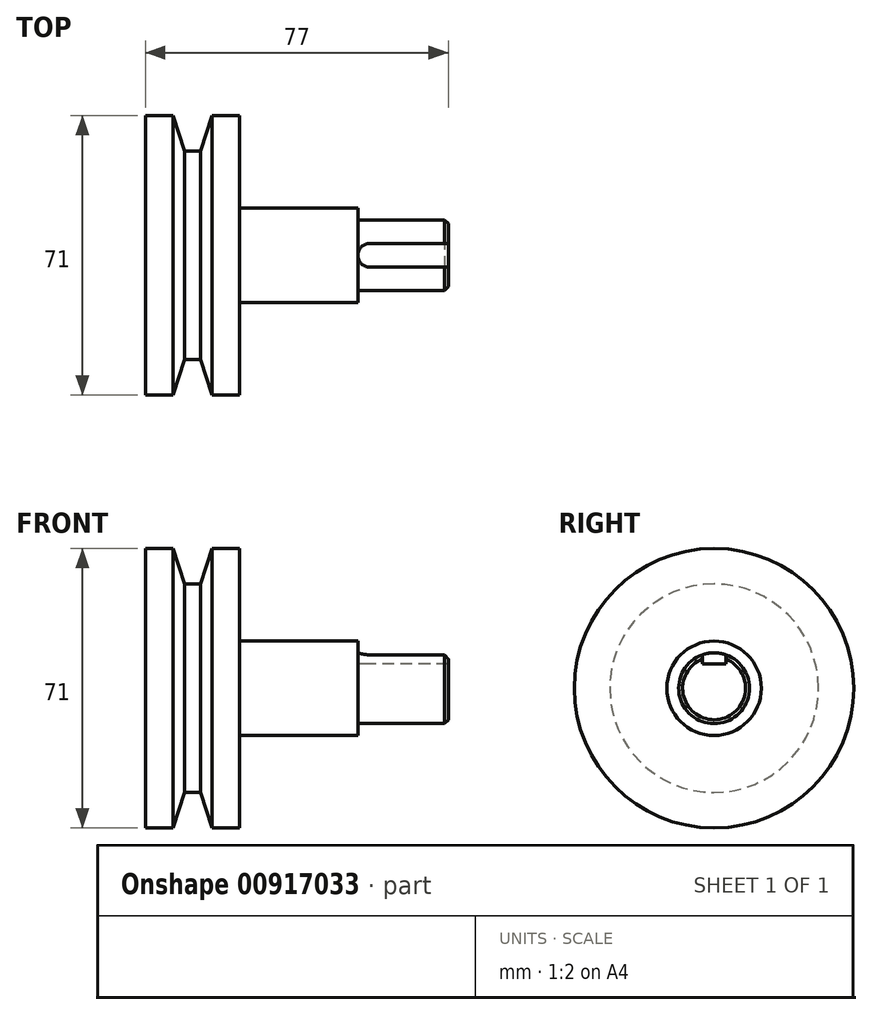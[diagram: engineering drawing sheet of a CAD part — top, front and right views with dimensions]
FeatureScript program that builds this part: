
annotation { "Feature Type Name" : "Feature", "Feature Type Description" : "" }
export const myFeature = defineFeature(function(context is Context, id is Id, definition is map)
    precondition{}
    {
        {
            var Q0;
            Q0=qCreatedBy(makeId("Front.planeOp"),FACE);
            var sketch = newSketch(context, id + "F0", { "sketchPlane" : qUnion([Q0])});
            skLineSegment(sketch, "E0", {"start": v(0, 0) * mm, "end": v(77, 0) * mm});
            skLineSegment(sketch, "E1", {"start": v(77, 0) * mm, "end": v(77, 9) * mm});
            skLineSegment(sketch, "E2", {"start": v(77, 9) * mm, "end": v(54, 9) * mm});
            skLineSegment(sketch, "E3", {"start": v(54, 9) * mm, "end": v(54, 12) * mm});
            skLineSegment(sketch, "E4", {"start": v(54, 12) * mm, "end": v(24, 12) * mm});
            skLineSegment(sketch, "E5", {"start": v(24, 12) * mm, "end": v(24, 35.5) * mm});
            skLineSegment(sketch, "E6", {"start": v(24, 35.5) * mm, "end": v(16.92, 35.5) * mm});
            skLineSegment(sketch, "E7", {"start": v(16.92, 35.5) * mm, "end": v(14, 26.5) * mm});
            skLineSegment(sketch, "E8", {"start": v(14, 26.5) * mm, "end": v(10, 26.5) * mm});
            skLineSegment(sketch, "E9", {"start": v(10, 26.5) * mm, "end": v(7.08, 35.5) * mm});
            skLineSegment(sketch, "E10", {"start": v(7.08, 35.5) * mm, "end": v(0, 35.5) * mm});
            skLineSegment(sketch, "E11", {"start": v(0, 35.5) * mm, "end": v(0, 0) * mm});
            skSolve(sketch);
        }
        {
            var Q0;
            Q0=makeQuery(id+"F0.imprint","IMPRINT",FACE,{"disambiguationData":[TD([[makeQuery(id+"F0.imprint","IMPRINT",EDGE,{"derivedFrom":sQuery(id+"F0.wireOp",EDGE,"E0")}),1.0]])]});
            var Q1;
            Q1=sQuery(id+"F0.wireOp",EDGE,"E0");
            revolve(context, id + "F1", {"surfaceOperationType" : NewSurfaceOperationType.NEW, "entities" : qUnion([Q0]), "axis" : qUnion([Q1]), "revolveType" : RevolveType.FULL});
        }
        {
            var Q0;
            Q0=qCreatedBy(makeId("Top.planeOp"),FACE);
            cPlane(context, id + "F2", {"entities" : qUnion([Q0]), "cplaneType" : CPlaneType.OFFSET, "offset" : 9 * mm, "width" : 150 * mm, "height" : 150 * mm});
        }
        {
            var Q0;
            Q0=qCreatedBy(id+"F2.planeOp",FACE);
            var sketch = newSketch(context, id + "F3", { "sketchPlane" : qUnion([Q0])});
            skLineSegment(sketch, "E12", {"start": v(77, -3) * mm, "end": v(77, 3) * mm});
            skLineSegment(sketch, "E13", {"start": v(77, 3) * mm, "end": v(57, 3) * mm});
            skLineSegment(sketch, "E14", {"start": v(77, -3) * mm, "end": v(57, -3) * mm});
            skArc(sketch, "E15", {"start": v(57, 3) * mm, "mid": v(54, 0) * mm, "end": v(57, -3) * mm});
            skSolve(sketch);
        }
        {
            var Q0;
            Q0=makeQuery(id+"F3.imprint","IMPRINT",FACE,{"disambiguationData":[TD([[makeQuery(id+"F3.imprint","IMPRINT",EDGE,{"derivedFrom":sQuery(id+"F3.wireOp",EDGE,"E12")}),1.0]])]});
            extrude(context, id + "F4", {"entities" : qUnion([Q0]), "operationType" : NewBodyOperationType.REMOVE, "oppositeDirection" : true, "depth" : 2.8 * mm, "offsetDistance" : 25 * mm});
        }
        {
            var Q0;
            Q0=makeQuery(id+"F1.opRevolve","SWEPT_EDGE",EDGE,{"disambiguationData":[OSD([sQuery(id+"F0.wireOp",EDGE,"E1"),sQuery(id+"F0.wireOp",EDGE,"E2")])]});
            chamfer(context, id + "F5", {"entities" : qUnion([Q0]), "width" : 1 * mm, "tangentPropagation" : true});
        }
    });
